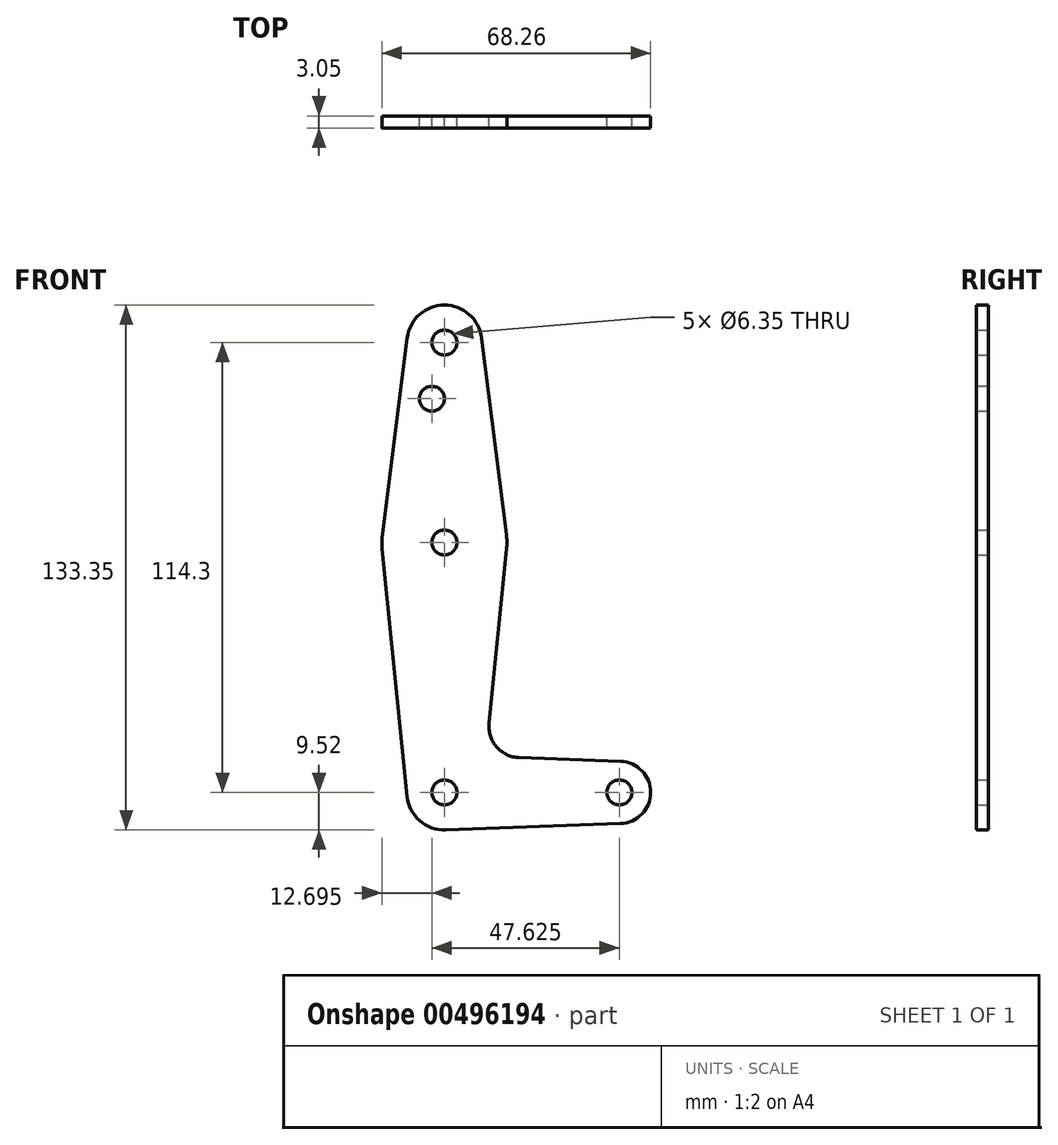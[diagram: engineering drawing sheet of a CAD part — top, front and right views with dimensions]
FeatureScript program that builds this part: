
annotation { "Feature Type Name" : "Feature", "Feature Type Description" : "" }
export const myFeature = defineFeature(function(context is Context, id is Id, definition is map)
    precondition{}
    {
        {
            var Q0;
            Q0=qCreatedBy(makeId("Front.planeOp"),FACE);
            var sketch = newSketch(context, id + "F0", { "sketchPlane" : qUnion([Q0])});
            skLineSegment(sketch, "E0", {"start": v(0, 114.3) * mm, "end": v(0, 0) * mm, "construction": true});
            skLineSegment(sketch, "E1", {"start": v(0, 0) * mm, "end": v(44.45, 0) * mm, "construction": true});
            skCircle(sketch, "E2", {"center": v(0, 114.3) * mm, "radius": 9.53 * mm});
            skCircle(sketch, "E3", {"center": v(0, 0) * mm, "radius": 9.53 * mm});
            skCircle(sketch, "E4", {"center": v(0, 63.5) * mm, "radius": 15.88 * mm});
            skCircle(sketch, "E5", {"center": v(44.45, 0) * mm, "radius": 7.94 * mm});
            skLineSegment(sketch, "E6", {"start": v(9.45, 115.5) * mm, "end": v(15.75, 65.48) * mm});
            skLineSegment(sketch, "E7", {"start": v(-9.45, 115.5) * mm, "end": v(-15.75, 65.48) * mm});
            skLineSegment(sketch, "E8", {"start": v(-15.8, 61.91) * mm, "end": v(-9.48, -0.95) * mm});
            skLineSegment(sketch, "E9", {"start": v(15.8, 61.91) * mm, "end": v(11.34, 17.6) * mm});
            skLineSegment(sketch, "E10", {"start": v(18.97, 8.85) * mm, "end": v(44.73, 7.93) * mm});
            skLineSegment(sketch, "E11", {"start": v(0.34, -9.52) * mm, "end": v(44.73, -7.93) * mm});
            skCircle(sketch, "E12", {"center": v(0, 63.5) * mm, "radius": 3.18 * mm});
            skCircle(sketch, "E13", {"center": v(0, 0) * mm, "radius": 3.18 * mm});
            skCircle(sketch, "E14", {"center": v(44.45, 0) * mm, "radius": 3.18 * mm});
            skCircle(sketch, "E15", {"center": v(0, 114.3) * mm, "radius": 3.18 * mm});
            skCircle(sketch, "E16", {"center": v(-3.18, 100.03) * mm, "radius": 3.18 * mm});
            skArc(sketch, "E17.filletArc", {"start": v(11.34, 17.6) * mm, "mid": v(13.26, 11.57) * mm, "end": v(18.97, 8.85) * mm});
            skSolve(sketch);
        }
        {
            var Q0;
            Q0 = qSketchRegion(id + "F0", true);
            extrude(context, id + "F1", {"entities" : qUnion([Q0]), "depth" : 3.05 * mm});
        }
    });
